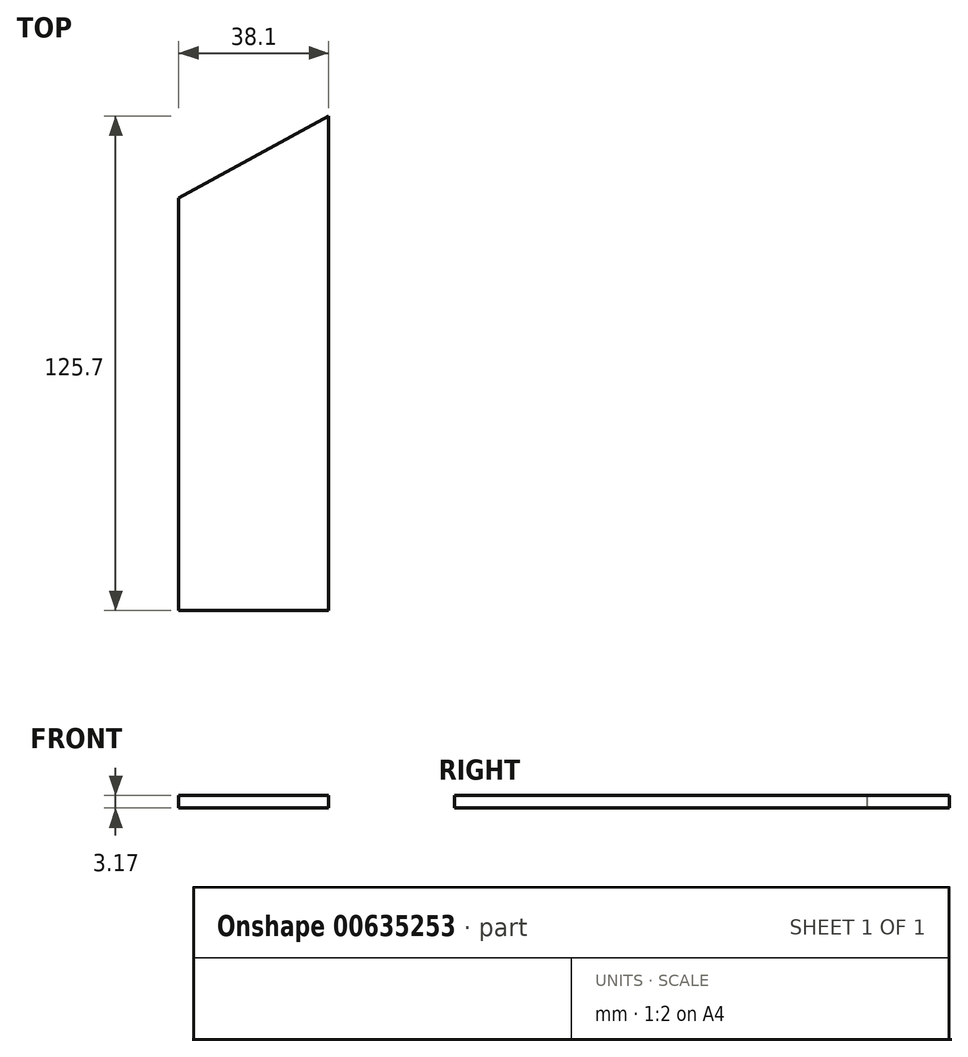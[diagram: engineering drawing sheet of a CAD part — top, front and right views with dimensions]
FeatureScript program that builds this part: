
annotation { "Feature Type Name" : "Feature", "Feature Type Description" : "" }
export const myFeature = defineFeature(function(context is Context, id is Id, definition is map)
    precondition{}
    {
        {
            var Q0;
            Q0=qCreatedBy(makeId("Top.planeOp"),FACE);
            var sketch = newSketch(context, id + "F0", { "sketchPlane" : qUnion([Q0])});
            skLineSegment(sketch, "E0.bottom", {"start": v(19.05, 52.39) * mm, "end": v(-19.05, 52.39) * mm});
            skLineSegment(sketch, "E0.top", {"start": v(19.05, -52.39) * mm, "end": v(-19.05, -52.39) * mm});
            skLineSegment(sketch, "E0.left", {"start": v(19.05, 52.39) * mm, "end": v(19.05, -52.39) * mm});
            skLineSegment(sketch, "E0.right", {"start": v(-19.05, 52.39) * mm, "end": v(-19.05, -52.39) * mm});
            skPoint(sketch, "E0.middle", {"position": v(0, 0) * mm});
            skLineSegment(sketch, "E1", {"start": v(-19.05, 52.39) * mm, "end": v(19.05, 73.31) * mm});
            skLineSegment(sketch, "E2", {"start": v(19.05, 73.31) * mm, "end": v(19.05, 52.39) * mm});
            skSolve(sketch);
        }
        {
            var Q0;
            Q0 = qSketchRegion(id + "F0", true);
            extrude(context, id + "F1", {"entities" : qUnion([Q0]), "depth" : 3.17 * mm, "offsetDistance" : 25.4 * mm});
        }
    });
